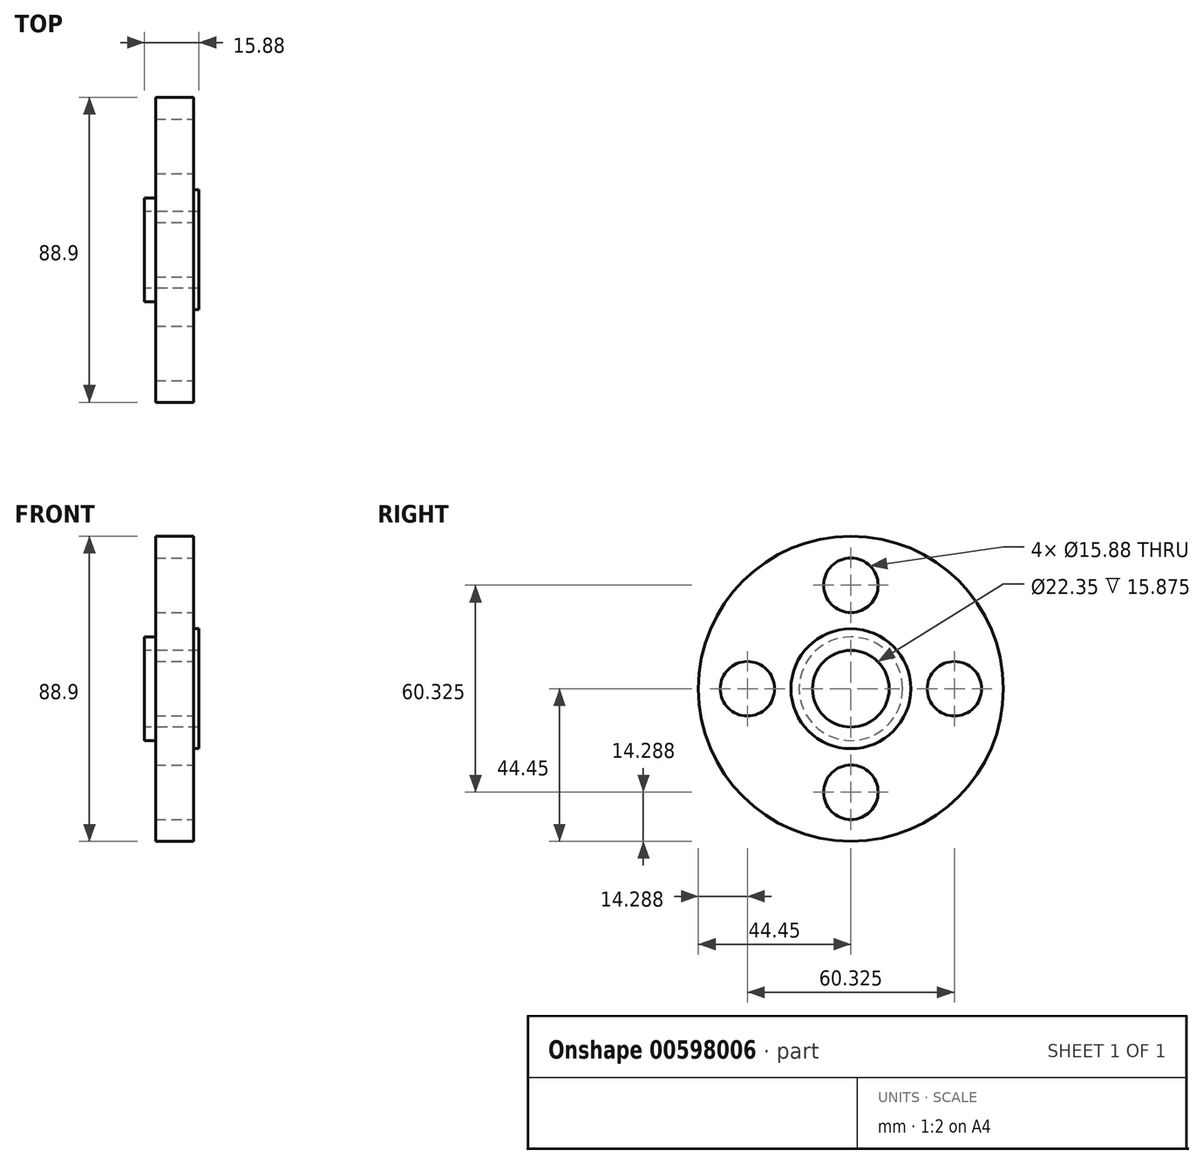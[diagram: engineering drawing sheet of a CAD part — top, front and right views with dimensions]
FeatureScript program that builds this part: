
annotation { "Feature Type Name" : "Feature", "Feature Type Description" : "" }
export const myFeature = defineFeature(function(context is Context, id is Id, definition is map)
    precondition{}
    {
        {
            var Q0;
            Q0=qCreatedBy(makeId("Front.planeOp"),FACE);
            var sketch = newSketch(context, id + "F0", { "sketchPlane" : qUnion([Q0])});
            skLineSegment(sketch, "E0", {"start": v(-23.02, 0) * mm, "end": v(23.79, 0) * mm, "construction": true});
            skLineSegment(sketch, "E1", {"start": v(0, 11.18) * mm, "end": v(15.88, 11.18) * mm});
            skLineSegment(sketch, "E2", {"start": v(15.88, 11.18) * mm, "end": v(15.88, 17.46) * mm});
            skLineSegment(sketch, "E3", {"start": v(15.88, 17.46) * mm, "end": v(14.35, 17.46) * mm});
            skLineSegment(sketch, "E4", {"start": v(14.35, 17.46) * mm, "end": v(14.35, 44.45) * mm});
            skLineSegment(sketch, "E5", {"start": v(14.35, 44.45) * mm, "end": v(3.25, 44.45) * mm});
            skLineSegment(sketch, "E6", {"start": v(3.25, 44.45) * mm, "end": v(3.25, 15.09) * mm});
            skLineSegment(sketch, "E7", {"start": v(3.25, 15.09) * mm, "end": v(0, 15.09) * mm});
            skLineSegment(sketch, "E8", {"start": v(0, 15.09) * mm, "end": v(0, 11.18) * mm});
            skSolve(sketch);
        }
        {
            var Q0;
            Q0 = qSketchRegion(id + "F0", true);
            var Q1;
            Q1=sQuery(id+"F0.wireOp",EDGE,"E0");
            revolve(context, id + "F1", {"entities" : qUnion([Q0]), "axis" : qUnion([Q1]), "revolveType" : RevolveType.FULL});
        }
        {
            var Q0;
            Q0=makeQuery(id+"F1.opRevolve","SWEPT_FACE",FACE,{"disambiguationData":[OSD([sQuery(id+"F0.wireOp",EDGE,"E4")])]});
            var sketch = newSketch(context, id + "F2", { "sketchPlane" : qUnion([Q0])});
            skCircle(sketch, "E9", {"center": v(0, 0) * mm, "radius": 30.16 * mm, "construction": true});
            skCircle(sketch, "E10", {"center": v(0, 30.16) * mm, "radius": 7.94 * mm});
            skCircle(sketch, "E11", {"center": v(0, -30.16) * mm, "radius": 7.94 * mm});
            skCircle(sketch, "E12", {"center": v(-30.16, 0) * mm, "radius": 7.94 * mm});
            skCircle(sketch, "E13.3.0", {"center": v(30.16, 0) * mm, "radius": 7.94 * mm});
            skSolve(sketch);
        }
        {
            var Q0;
            Q0 = qSketchRegion(id + "F2", true);
            extrude(context, id + "F3", {"entities" : qUnion([Q0]), "operationType" : NewBodyOperationType.REMOVE, "endBound" : BoundingType.THROUGH_ALL, "oppositeDirection" : true, "depth" : 25.4 * mm, "offsetDistance" : 25.4 * mm});
        }
    });
